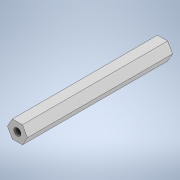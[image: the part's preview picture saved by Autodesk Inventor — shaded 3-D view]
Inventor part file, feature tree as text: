
AUTODESK INVENTOR PART (.ipt)
format: ipt  version: 2020 (Build 240168000, 168)  size: 109,568 bytes
history: native  units: in
note: dims shown in document units (in); Inventor stores cm internally (conversion verified against a paired STEP export)
features: sketch x2, other x1, extrude x1, hole x1, plane x1, mirror x1, projected_geometry x1
ambient origin geometry x8: Origin, YZ Plane, XZ Plane, XY Plane, X Axis, Y Axis, Z Axis, Center Point
bodies: Solid1 (feature_tree)
feature tree (8):
  other  "Wurth 970500361"
  extrude  "Extrusion1"  Depth=1.9685in TaperAngle=0.0deg
  hole  "Hole1"  [1 undecoded]
  plane  "Work Plane1"
  mirror  "Mirror1"
  sketch  "Sketch1"  dims[d0=0.2362in d1=1.9685in d2=0.0in]
  sketch  "Sketch2"  dims[d3=0.0968in d4=0.2953in d5=0.1575in d6=0.0787in d7=90.0deg d8=0.2953in d9=0.0in]
  projected_geometry  "Projected Loop1"
note: 1 required parameter value undecoded (feature->parameter linkage not recoverable at this tier; creation-order binding heuristic only, values carry confidence <= 0.55)
